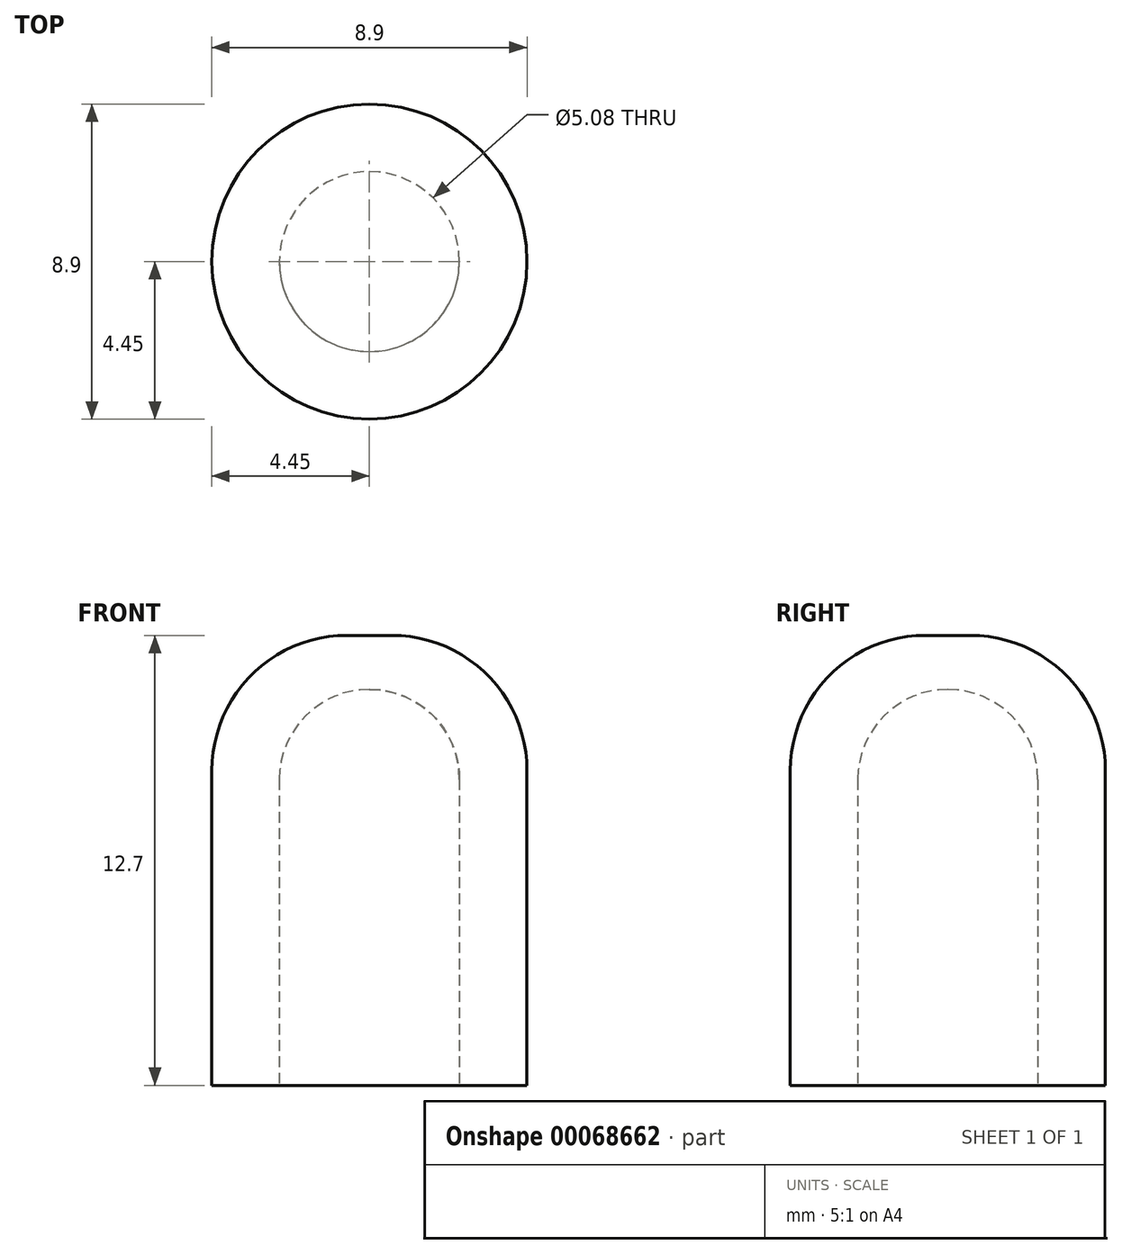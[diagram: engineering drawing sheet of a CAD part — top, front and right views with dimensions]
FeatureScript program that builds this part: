
annotation { "Feature Type Name" : "Feature", "Feature Type Description" : "" }
export const myFeature = defineFeature(function(context is Context, id is Id, definition is map)
    precondition{}
    {
        {
            var Q0;
            Q0=qCreatedBy(makeId("Top.planeOp"),FACE);
            var sketch = newSketch(context, id + "F0", { "sketchPlane" : qUnion([Q0])});
            skCircle(sketch, "E0", {"center": v(0, 0) * mm, "radius": 4.44 * mm});
            skSolve(sketch);
        }
        {
            var Q0;
            Q0 = qSketchRegion(id + "F0", true);
            extrude(context, id + "F1", {"entities" : qUnion([Q0]), "depth" : 12.7 * mm});
        }
        {
            var Q0;
            Q0=makeQuery(id+"F1.opExtrude","CAP_EDGE",EDGE,{"disambiguationData":[OSD([sQuery(id+"F0.wireOp",EDGE,"E0")])],"isStart":false});
            fillet(context, id + "F2", {"entities" : qUnion([Q0]), "radius" : 3.8 * mm, "tangentPropagation" : true, "allowEdgeOverflow" : false});
        }
        {
            var Q0;
            Q0=qCreatedBy(makeId("Front.planeOp"),FACE);
            var sketch = newSketch(context, id + "F3", { "sketchPlane" : qUnion([Q0])});
            skLineSegment(sketch, "E1", {"start": v(0, 0) * mm, "end": v(-2.54, 0) * mm});
            skLineSegment(sketch, "E2", {"start": v(-2.54, 0) * mm, "end": v(-2.54, 8.64) * mm});
            skLineSegment(sketch, "E3", {"start": v(-2.54, 8.64) * mm, "end": v(0, 8.64) * mm, "construction": true});
            skLineSegment(sketch, "E4", {"start": v(0, 8.64) * mm, "end": v(0, 0) * mm});
            skArc(sketch, "E5", {"start": v(0, 11.18) * mm, "mid": v(-1.8, 10.43) * mm, "end": v(-2.54, 8.64) * mm});
            skLineSegment(sketch, "E6", {"start": v(0, 8.64) * mm, "end": v(0, 11.18) * mm});
            skSolve(sketch);
        }
        {
            var Q0;
            Q0 = qSketchRegion(id + "F3", true);
            var Q1;
            Q1=sQuery(id+"F3.wireOp",EDGE,"E4");
            revolve(context, id + "F4", {"operationType" : NewBodyOperationType.REMOVE, "entities" : qUnion([Q0]), "axis" : qUnion([Q1]), "revolveType" : RevolveType.FULL, "oppositeDirection" : true});
        }
    });
